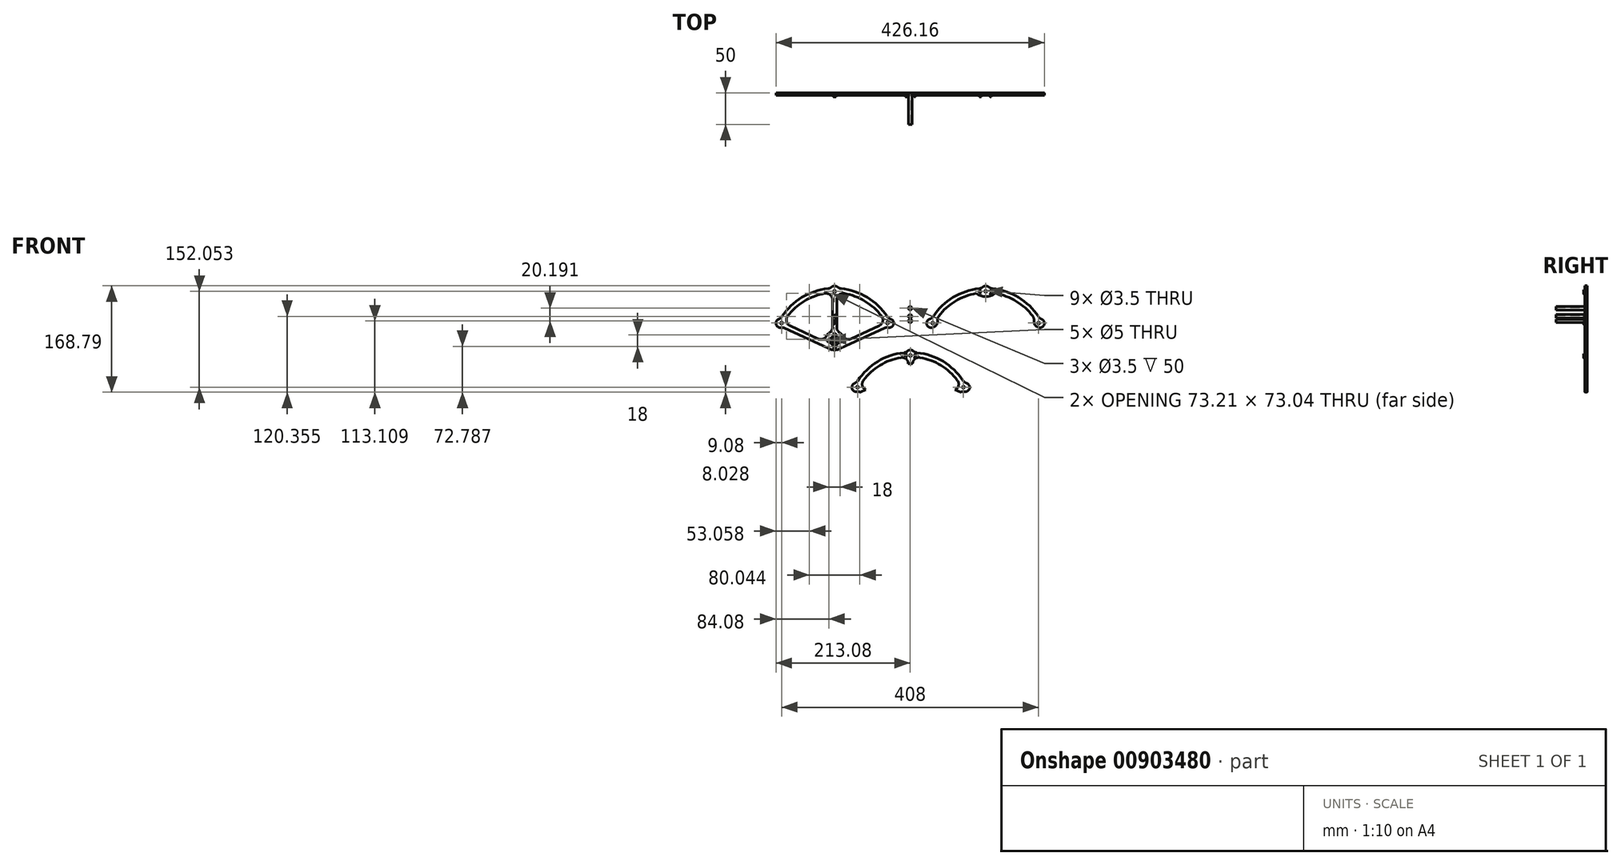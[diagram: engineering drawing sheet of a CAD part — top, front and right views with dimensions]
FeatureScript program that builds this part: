
annotation { "Feature Type Name" : "Feature", "Feature Type Description" : "" }
export const myFeature = defineFeature(function(context is Context, id is Id, definition is map)
    precondition{}
    {
        {
            var Q0;
            Q0=qCreatedBy(makeId("Front.planeOp"),FACE);
            var sketch = newSketch(context, id + "F0", { "sketchPlane" : qUnion([Q0])});
            skLineSegment(sketch, "E0", {"start": v(-146.14, -35.75) * mm, "end": v(-190.85, -14.94) * mm});
            skLineSegment(sketch, "E1", {"start": v(-93.86, -35.75) * mm, "end": v(-49.15, -14.94) * mm});
            skArc(sketch, "E2", {"start": v(-45.36, 0.11) * mm, "mid": v(-71.63, 23.96) * mm, "end": v(-104.9, 36.26) * mm});
            skArc(sketch, "E3", {"start": v(-135.1, 36.26) * mm, "mid": v(-168.37, 23.96) * mm, "end": v(-194.64, 0.11) * mm});
            skArc(sketch, "E4", {"start": v(-194.64, 0.11) * mm, "mid": v(-196.33, -8.32) * mm, "end": v(-190.85, -14.94) * mm});
            skArc(sketch, "E5", {"start": v(-49.15, -14.94) * mm, "mid": v(-43.67, -8.32) * mm, "end": v(-45.36, 0.11) * mm});
            skArc(sketch, "E6", {"start": v(-106.85, -31.5) * mm, "mid": v(-101.2, -36.19) * mm, "end": v(-93.86, -35.75) * mm});
            skArc(sketch, "E7", {"start": v(-146.14, -35.75) * mm, "mid": v(-138.8, -36.19) * mm, "end": v(-133.15, -31.5) * mm});
            skArc(sketch, "E8", {"start": v(-123.48, 26.4) * mm, "mid": v(-127.02, 34.02) * mm, "end": v(-135.1, 36.26) * mm});
            skArc(sketch, "E9", {"start": v(-104.9, 36.26) * mm, "mid": v(-112.98, 34.02) * mm, "end": v(-116.52, 26.4) * mm});
            skArc(sketch, "E10", {"start": v(-115.3, 46.48) * mm, "mid": v(-120, 48.29) * mm, "end": v(-124.7, 46.48) * mm});
            skArc(sketch, "E11", {"start": v(-130.36, 43.95) * mm, "mid": v(-127.33, 44.77) * mm, "end": v(-124.7, 46.48) * mm});
            skArc(sketch, "E12", {"start": v(-115.3, 46.48) * mm, "mid": v(-112.67, 44.77) * mm, "end": v(-109.64, 43.95) * mm});
            skArc(sketch, "E13", {"start": v(-130.36, 43.95) * mm, "mid": v(-172.02, 29.93) * mm, "end": v(-203.67, -0.57) * mm});
            skLineSegment(sketch, "E14", {"start": v(-116.58, -17.6) * mm, "end": v(-116.52, 26.4) * mm});
            skLineSegment(sketch, "E15", {"start": v(-123.48, 26.4) * mm, "end": v(-123.42, -17.6) * mm});
            skArc(sketch, "E16", {"start": v(-106.85, -31.5) * mm, "mid": v(-109.06, -28.45) * mm, "end": v(-111.95, -26.06) * mm});
            skArc(sketch, "E17", {"start": v(-128.05, -26.06) * mm, "mid": v(-130.94, -28.45) * mm, "end": v(-133.15, -31.5) * mm});
            skArc(sketch, "E18", {"start": v(-36.55, -0.24) * mm, "mid": v(-68.15, 30.03) * mm, "end": v(-109.64, 43.95) * mm});
            skArc(sketch, "E19", {"start": v(-34.39, -17.87) * mm, "mid": v(-26.28, -12.65) * mm, "end": v(-31.08, -4.29) * mm});
            skArc(sketch, "E20", {"start": v(-208.52, -4.44) * mm, "mid": v(-212.85, -12.76) * mm, "end": v(-205.02, -17.92) * mm});
            skArc(sketch, "E21", {"start": v(-208.52, -4.44) * mm, "mid": v(-205.79, -2.9) * mm, "end": v(-203.67, -0.57) * mm});
            skArc(sketch, "E22", {"start": v(-199.29, -18.74) * mm, "mid": v(-202.1, -17.9) * mm, "end": v(-205.02, -17.92) * mm});
            skArc(sketch, "E23", {"start": v(-34.39, -17.87) * mm, "mid": v(-37.5, -17.77) * mm, "end": v(-40.49, -18.63) * mm});
            skArc(sketch, "E24", {"start": v(-36.55, -0.24) * mm, "mid": v(-34.17, -2.75) * mm, "end": v(-31.08, -4.29) * mm});
            skArc(sketch, "E25", {"start": v(-128.05, -26.06) * mm, "mid": v(-124.65, -22.43) * mm, "end": v(-123.42, -17.6) * mm});
            skArc(sketch, "E26", {"start": v(-116.58, -17.6) * mm, "mid": v(-115.35, -22.43) * mm, "end": v(-111.95, -26.06) * mm});
            skCircle(sketch, "E27", {"center": v(-120, 39.58) * mm, "radius": 1.75 * mm});
            skCircle(sketch, "E28", {"center": v(-115.62, -43.1) * mm, "radius": 1.25 * mm});
            skCircle(sketch, "E29", {"center": v(-204, -10.71) * mm, "radius": 1.75 * mm});
            skCircle(sketch, "E30", {"center": v(-115.62, -34.33) * mm, "radius": 1.25 * mm});
            skCircle(sketch, "E31", {"center": v(-124.38, -43.1) * mm, "radius": 1.25 * mm});
            skArc(sketch, "E32", {"start": v(-34.39, -17.87) * mm, "mid": v(-37.55, -17.78) * mm, "end": v(-40.58, -18.68) * mm});
            skCircle(sketch, "E33", {"center": v(-124.38, -34.33) * mm, "radius": 1.25 * mm});
            skCircle(sketch, "E34", {"center": v(-36, -10.71) * mm, "radius": 1.75 * mm});
            skCircle(sketch, "E35", {"center": v(-120, -38.71) * mm, "radius": 2.5 * mm});
            skArc(sketch, "E36", {"start": v(104.9, 36.26) * mm, "mid": v(71.63, 23.96) * mm, "end": v(45.36, 0.11) * mm});
            skArc(sketch, "E37", {"start": v(194.64, 0.11) * mm, "mid": v(168.37, 23.96) * mm, "end": v(135.1, 36.26) * mm});
            skArc(sketch, "E38", {"start": v(124.7, 46.48) * mm, "mid": v(120, 48.29) * mm, "end": v(115.3, 46.48) * mm});
            skArc(sketch, "E39", {"start": v(124.7, 46.48) * mm, "mid": v(127.33, 44.77) * mm, "end": v(130.36, 43.95) * mm});
            skArc(sketch, "E40", {"start": v(109.64, 43.95) * mm, "mid": v(112.67, 44.77) * mm, "end": v(115.3, 46.48) * mm});
            skArc(sketch, "E41", {"start": v(203.67, -0.57) * mm, "mid": v(172.02, 29.93) * mm, "end": v(130.36, 43.95) * mm});
            skArc(sketch, "E42", {"start": v(109.64, 43.95) * mm, "mid": v(68.15, 30.03) * mm, "end": v(36.55, -0.24) * mm});
            skArc(sketch, "E43", {"start": v(31.08, -4.29) * mm, "mid": v(26.28, -12.65) * mm, "end": v(34.39, -17.87) * mm});
            skArc(sketch, "E44", {"start": v(205.02, -17.92) * mm, "mid": v(212.85, -12.76) * mm, "end": v(208.52, -4.44) * mm});
            skArc(sketch, "E45", {"start": v(203.67, -0.57) * mm, "mid": v(205.79, -2.9) * mm, "end": v(208.52, -4.44) * mm});
            skArc(sketch, "E46", {"start": v(31.08, -4.29) * mm, "mid": v(34.17, -2.75) * mm, "end": v(36.55, -0.24) * mm});
            skCircle(sketch, "E47", {"center": v(120, 39.58) * mm, "radius": 1.75 * mm});
            skArc(sketch, "E48", {"start": v(205.02, -17.92) * mm, "mid": v(205.02, -17.92) * mm, "end": v(205.01, -17.92) * mm});
            skCircle(sketch, "E49", {"center": v(204, -10.71) * mm, "radius": 1.75 * mm});
            skArc(sketch, "E50", {"start": v(31.08, -4.29) * mm, "mid": v(26.32, -12.82) * mm, "end": v(34.72, -17.8) * mm});
            skCircle(sketch, "E51", {"center": v(36, -10.71) * mm, "radius": 1.75 * mm});
            skArc(sketch, "E52", {"start": v(196.57, -6.95) * mm, "mid": v(198.59, -14.13) * mm, "end": v(205.01, -17.92) * mm});
            skArc(sketch, "E53", {"start": v(34.61, -17.83) * mm, "mid": v(41.26, -14.16) * mm, "end": v(43.42, -6.88) * mm});
            skArc(sketch, "E54", {"start": v(45.36, 0.11) * mm, "mid": v(43.74, -3.2) * mm, "end": v(43.42, -6.88) * mm});
            skArc(sketch, "E55", {"start": v(196.57, -6.95) * mm, "mid": v(196.27, -3.24) * mm, "end": v(194.64, 0.11) * mm});
            skArc(sketch, "E56", {"start": v(104.9, 36.26) * mm, "mid": v(120, 31.29) * mm, "end": v(135.1, 36.26) * mm});
            skCircle(sketch, "E57", {"center": v(-120, -29.71) * mm, "radius": 2.5 * mm});
            skCircle(sketch, "E58", {"center": v(-129, -38.71) * mm, "radius": 2.5 * mm});
            skCircle(sketch, "E59", {"center": v(-111, -38.71) * mm, "radius": 2.5 * mm});
            skCircle(sketch, "E60", {"center": v(-120, -47.71) * mm, "radius": 2.5 * mm});
            skLineSegment(sketch, "E61", {"start": v(-199.29, -18.74) * mm, "end": v(-130, -50.71) * mm});
            skLineSegment(sketch, "E62", {"start": v(-40.58, -18.68) * mm, "end": v(-110, -50.71) * mm});
            skArc(sketch, "E63", {"start": v(-130, -50.71) * mm, "mid": v(-120, -53.4) * mm, "end": v(-110, -50.71) * mm});
            skArc(sketch, "E64", {"start": v(75.08, -101.65) * mm, "mid": v(48.82, -77.8) * mm, "end": v(15.55, -65.5) * mm});
            skArc(sketch, "E65", {"start": v(-14.66, -65.5) * mm, "mid": v(-47.93, -77.8) * mm, "end": v(-74.19, -101.65) * mm});
            skArc(sketch, "E66", {"start": v(-74.19, -101.65) * mm, "mid": v(-75.88, -110.08) * mm, "end": v(-70.4, -116.7) * mm});
            skArc(sketch, "E67", {"start": v(71.3, -116.7) * mm, "mid": v(76.77, -110.08) * mm, "end": v(75.08, -101.65) * mm});
            skArc(sketch, "E68", {"start": v(-3.04, -75.35) * mm, "mid": v(-6.57, -67.74) * mm, "end": v(-14.66, -65.5) * mm});
            skArc(sketch, "E69", {"start": v(15.55, -65.5) * mm, "mid": v(7.46, -67.74) * mm, "end": v(3.93, -75.35) * mm});
            skArc(sketch, "E70", {"start": v(5.14, -55.28) * mm, "mid": v(0.45, -53.47) * mm, "end": v(-4.25, -55.28) * mm});
            skArc(sketch, "E71", {"start": v(-9.92, -57.8) * mm, "mid": v(-6.88, -57) * mm, "end": v(-4.25, -55.28) * mm});
            skArc(sketch, "E72", {"start": v(5.14, -55.28) * mm, "mid": v(7.77, -57) * mm, "end": v(10.8, -57.8) * mm});
            skArc(sketch, "E73", {"start": v(-9.92, -57.8) * mm, "mid": v(-51.57, -71.83) * mm, "end": v(-83.22, -102.33) * mm});
            skArc(sketch, "E74", {"start": v(83.9, -102) * mm, "mid": v(52.3, -71.73) * mm, "end": v(10.8, -57.8) * mm});
            skArc(sketch, "E75", {"start": v(86.06, -119.63) * mm, "mid": v(94.17, -114.41) * mm, "end": v(89.37, -106.05) * mm});
            skArc(sketch, "E76", {"start": v(-88.08, -106.2) * mm, "mid": v(-92.4, -114.52) * mm, "end": v(-84.58, -119.68) * mm});
            skArc(sketch, "E77", {"start": v(-88.08, -106.2) * mm, "mid": v(-85.34, -104.65) * mm, "end": v(-83.22, -102.33) * mm});
            skArc(sketch, "E78", {"start": v(-78.84, -120.5) * mm, "mid": v(-81.65, -119.66) * mm, "end": v(-84.58, -119.68) * mm});
            skArc(sketch, "E79", {"start": v(86.06, -119.63) * mm, "mid": v(82.95, -119.53) * mm, "end": v(79.96, -120.4) * mm});
            skArc(sketch, "E80", {"start": v(83.9, -102) * mm, "mid": v(86.28, -104.5) * mm, "end": v(89.37, -106.05) * mm});
            skCircle(sketch, "E81", {"center": v(0.45, -62.18) * mm, "radius": 1.75 * mm});
            skCircle(sketch, "E82", {"center": v(-83.55, -112.47) * mm, "radius": 1.75 * mm});
            skArc(sketch, "E83", {"start": v(86.06, -119.63) * mm, "mid": v(82.9, -119.54) * mm, "end": v(79.87, -120.44) * mm});
            skCircle(sketch, "E84", {"center": v(84.45, -112.47) * mm, "radius": 1.75 * mm});
            skLineSegment(sketch, "E85", {"start": v(-78.84, -120.5) * mm, "end": v(-70.4, -116.7) * mm});
            skLineSegment(sketch, "E86", {"start": v(-3.04, -75.35) * mm, "end": v(3.93, -75.35) * mm});
            skLineSegment(sketch, "E87", {"start": v(79.96, -120.4) * mm, "end": v(71.3, -116.7) * mm});
            skSolve(sketch);
        }
        {
            var Q0;
            Q0 = qSketchRegion(id + "F0", true);
            extrude(context, id + "F1", {"entities" : qUnion([Q0]), "depth" : 4 * mm, "offsetDistance" : 25 * mm});
        }
        {
            var Q0;
            Q0=qCreatedBy(makeId("Front.planeOp"),FACE);
            var sketch = newSketch(context, id + "F2", { "sketchPlane" : qUnion([Q0])});
            skText(sketch, "E88", { "text": "K", "fontName": "OpenSans-Regular.ttf"});
            skText(sketch, "E89", { "text": "J", "fontName": "OpenSans-Regular.ttf"});
            const initialGuessF2  = {"E88": [-0.12257, -0.00237, 1, 0, 0.00555], "E89": [-0.12116, -0.011, 1, 0, 0.00637]};
            skSetInitialGuess(sketch, initialGuessF2);
            skSolve(sketch);
        }
        {
            var Q0;
            Q0 = qSketchRegion(id + "F2", true);
            extrude(context, id + "F3", {"entities" : qUnion([Q0]), "operationType" : NewBodyOperationType.ADD, "depth" : 6 * mm, "offsetDistance" : 25 * mm});
        }
        {
            var Q0;
            Q0=qCreatedBy(makeId("Front.planeOp"),FACE);
            var sketch = newSketch(context, id + "F4", { "sketchPlane" : qUnion([Q0])});
            skText(sketch, "E90", { "text": "K", "fontName": "OpenSans-Regular.ttf"});
            skText(sketch, "E91", { "text": "J", "fontName": "OpenSans-Regular.ttf"});
            const initialGuessF4  = {"E90": [0.10913, 0.03702, 1, 0, 0.0043], "E91": [0.12726, 0.03688, 1, 0, 0.0054]};
            skSetInitialGuess(sketch, initialGuessF4);
            skSolve(sketch);
        }
        {
            var Q0;
            Q0 = qSketchRegion(id + "F4", true);
            extrude(context, id + "F5", {"entities" : qUnion([Q0]), "operationType" : NewBodyOperationType.ADD, "depth" : 6 * mm, "offsetDistance" : 25 * mm});
        }
        {
            var Q0;
            Q0=qCreatedBy(makeId("Front.planeOp"),FACE);
            var sketch = newSketch(context, id + "F6", { "sketchPlane" : qUnion([Q0])});
            skCircle(sketch, "E92", {"center": v(0, 0) * mm, "radius": 2.75 * mm});
            skCircle(sketch, "E93", {"center": v(0, 0) * mm, "radius": 1.75 * mm});
            skCircle(sketch, "E94", {"center": v(0, 12.8) * mm, "radius": 2.75 * mm});
            skCircle(sketch, "E95", {"center": v(0, 12.8) * mm, "radius": 1.75 * mm});
            skCircle(sketch, "E96", {"center": v(0, -7.4) * mm, "radius": 2.75 * mm});
            skCircle(sketch, "E97", {"center": v(0, -7.4) * mm, "radius": 1.75 * mm});
            skCircle(sketch, "E98", {"center": v(0, -20.44) * mm, "radius": 2.75 * mm});
            skCircle(sketch, "E99", {"center": v(0, -20.44) * mm, "radius": 1.75 * mm});
            skSolve(sketch);
        }
        {
            var Q0;
            Q0 = qSketchRegion(id + "F6", true);
            extrude(context, id + "F7", {"entities" : qUnion([Q0]), "depth" : 50 * mm, "offsetDistance" : 25 * mm});
        }
        {
            var Q0;
            Q0=makeQuery(id+"F7.opExtrude","SWEPT_BODY",BODY,{"disambiguationData":[OSD([sQuery(id+"F6.wireOp",EDGE,"E98"),sQuery(id+"F6.wireOp",EDGE,"E99")])]});
            deleteBodies(context, id + "F8", {"entities" : qUnion([Q0])});
        }
        {
            var Q0;
            Q0=makeQuery(id+"F1.opExtrude","CAP_FACE",FACE,{"disambiguationData":[OSD([sQuery(id+"F0.wireOp",EDGE,"E81"),sQuery(id+"F0.wireOp",EDGE,"E82"),sQuery(id+"F0.wireOp",EDGE,"E64"),sQuery(id+"F0.wireOp",EDGE,"E65"),sQuery(id+"F0.wireOp",EDGE,"E66"),sQuery(id+"F0.wireOp",EDGE,"E67"),sQuery(id+"F0.wireOp",EDGE,"E68"),sQuery(id+"F0.wireOp",EDGE,"E69"),sQuery(id+"F0.wireOp",EDGE,"E77"),sQuery(id+"F0.wireOp",EDGE,"E78"),sQuery(id+"F0.wireOp",EDGE,"E79"),sQuery(id+"F0.wireOp",EDGE,"E80"),sQuery(id+"F0.wireOp",EDGE,"E76"),sQuery(id+"F0.wireOp",EDGE,"E74"),sQuery(id+"F0.wireOp",EDGE,"E75"),sQuery(id+"F0.wireOp",EDGE,"E70"),sQuery(id+"F0.wireOp",EDGE,"E71"),sQuery(id+"F0.wireOp",EDGE,"E72"),sQuery(id+"F0.wireOp",EDGE,"E73"),sQuery(id+"F0.wireOp",EDGE,"E84"),sQuery(id+"F0.wireOp",EDGE,"E85"),sQuery(id+"F0.wireOp",EDGE,"E86"),sQuery(id+"F0.wireOp",EDGE,"E87")])],"isStart":false});
            var sketch = newSketch(context, id + "F9", { "sketchPlane" : qUnion([Q0])});
            skText(sketch, "E100", { "text": "K", "fontName": "OpenSans-Regular.ttf"});
            skText(sketch, "E101", { "text": "J", "fontName": "OpenSans-Regular.ttf"});
            const initialGuessF9  = {"E100": [-0.00868, -0.06464, 1, 0, 0.00487], "E101": [0.00711, -0.06455, 1, 0, 0.00492]};
            skSetInitialGuess(sketch, initialGuessF9);
            skSolve(sketch);
        }
        {
            var Q0;
            Q0 = qSketchRegion(id + "F9", true);
            extrude(context, id + "F10", {"entities" : qUnion([Q0]), "operationType" : NewBodyOperationType.ADD, "depth" : 2 * mm, "offsetDistance" : 25 * mm});
        }
    });
